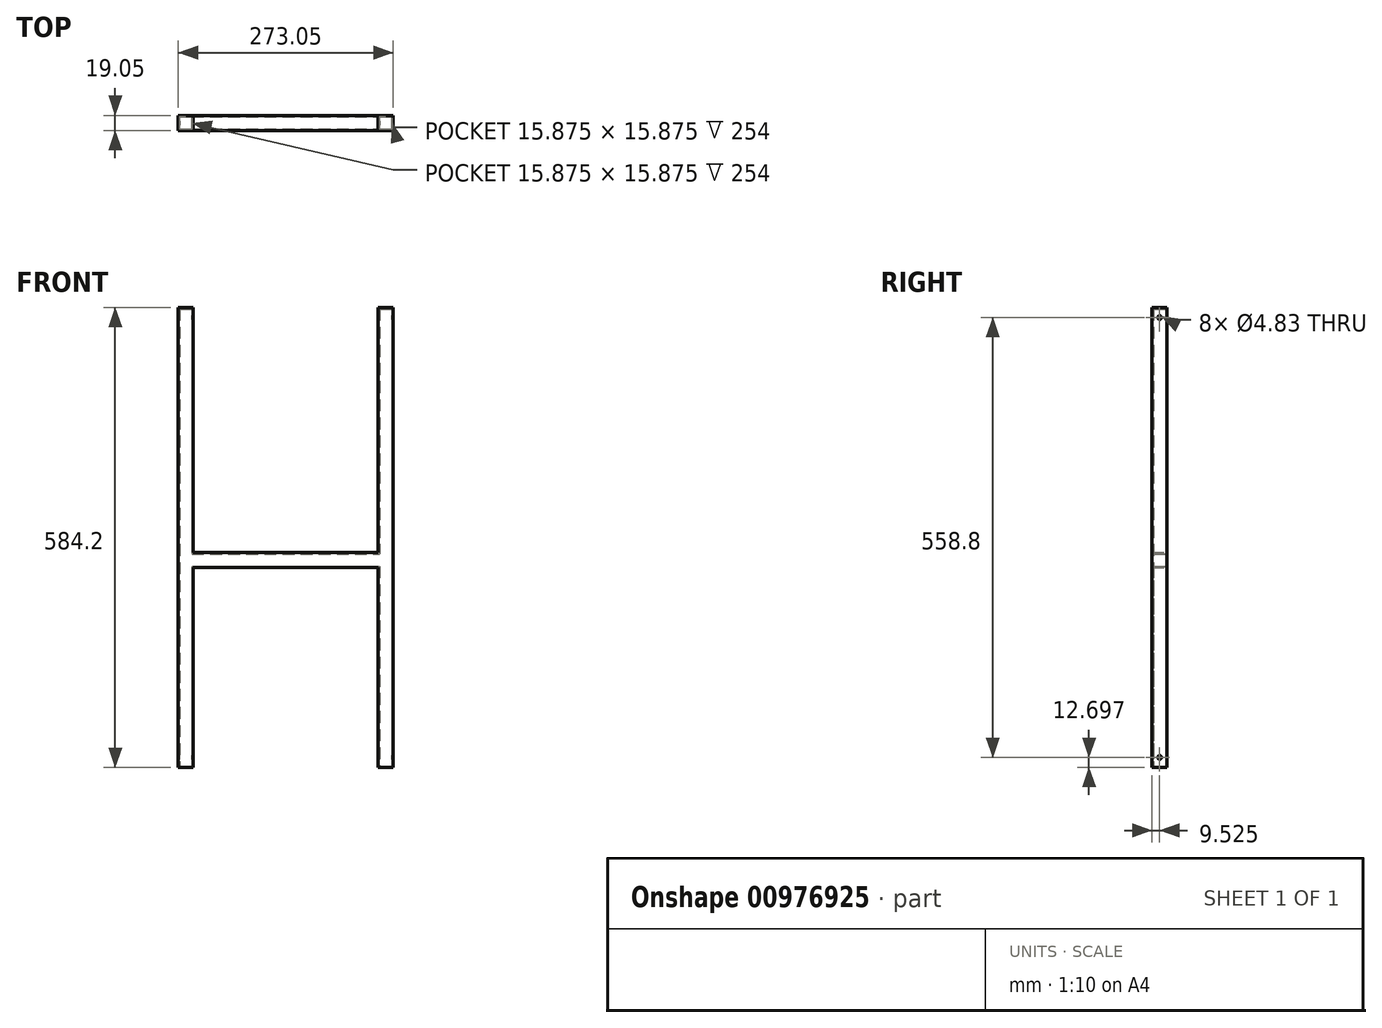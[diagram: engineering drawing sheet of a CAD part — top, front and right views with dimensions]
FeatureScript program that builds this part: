
annotation { "Feature Type Name" : "Feature", "Feature Type Description" : "" }
export const myFeature = defineFeature(function(context is Context, id is Id, definition is map)
    precondition{}
    {
        {
            var Q0;
            Q0=qCreatedBy(makeId("Front.planeOp"),FACE);
            var sketch = newSketch(context, id + "F0", { "sketchPlane" : qUnion([Q0])});
            skLineSegment(sketch, "E0.bottom", {"start": v(-125.54, 190.19) * mm, "end": v(-106.49, 190.19) * mm});
            skLineSegment(sketch, "E0.top", {"start": v(-125.54, -394.01) * mm, "end": v(-106.49, -394.01) * mm});
            skLineSegment(sketch, "E0.left", {"start": v(-125.54, 190.19) * mm, "end": v(-125.54, -394.01) * mm});
            skLineSegment(sketch, "E0.right", {"start": v(-106.49, 190.19) * mm, "end": v(-106.49, -394.01) * mm});
            skLineSegment(sketch, "E1.bottom", {"start": v(128.46, 190.19) * mm, "end": v(147.51, 190.19) * mm});
            skLineSegment(sketch, "E1.top", {"start": v(128.46, -394.01) * mm, "end": v(147.51, -394.01) * mm});
            skLineSegment(sketch, "E1.left", {"start": v(128.46, 190.19) * mm, "end": v(128.46, -394.01) * mm});
            skLineSegment(sketch, "E1.right", {"start": v(147.51, 190.19) * mm, "end": v(147.51, -394.01) * mm});
            skLineSegment(sketch, "E2.bottom", {"start": v(-106.49, -120.96) * mm, "end": v(128.46, -120.96) * mm});
            skLineSegment(sketch, "E2.top", {"start": v(-106.49, -140.01) * mm, "end": v(128.46, -140.01) * mm});
            skLineSegment(sketch, "E2.left", {"start": v(-106.49, -120.96) * mm, "end": v(-106.49, -140.01) * mm});
            skLineSegment(sketch, "E2.right", {"start": v(128.46, -120.96) * mm, "end": v(128.46, -140.01) * mm});
            skSolve(sketch);
        }
        {
            var Q0;
            Q0 = qSketchRegion(id + "F0", true);
            extrude(context, id + "F1", {"entities" : qUnion([Q0]), "depth" : 19.05 * mm, "offsetDistance" : 25.4 * mm});
        }
        {
            var Q0;
            Q0=makeQuery(id+"F1.opExtrude","CAP_FACE",FACE,{"disambiguationData":[OSD([sQuery(id+"F0.wireOp",EDGE,"E0.bottom"),sQuery(id+"F0.wireOp",EDGE,"E0.top"),sQuery(id+"F0.wireOp",EDGE,"E0.left"),sQuery(id+"F0.wireOp",EDGE,"E0.right"),sQuery(id+"F0.wireOp",EDGE,"E1.bottom"),sQuery(id+"F0.wireOp",EDGE,"E1.top"),sQuery(id+"F0.wireOp",EDGE,"E1.left"),sQuery(id+"F0.wireOp",EDGE,"E1.right"),sQuery(id+"F0.wireOp",EDGE,"E2.bottom"),sQuery(id+"F0.wireOp",EDGE,"E2.top")])],"isStart":true});
            var Q1;
            Q1=makeQuery(id+"F1.opExtrude","SWEPT_BODY",BODY,{"disambiguationData":[OSD([sQuery(id+"F0.wireOp",EDGE,"E0.bottom"),sQuery(id+"F0.wireOp",EDGE,"E0.top"),sQuery(id+"F0.wireOp",EDGE,"E0.left"),sQuery(id+"F0.wireOp",EDGE,"E0.right"),sQuery(id+"F0.wireOp",EDGE,"E1.bottom"),sQuery(id+"F0.wireOp",EDGE,"E1.top"),sQuery(id+"F0.wireOp",EDGE,"E1.left"),sQuery(id+"F0.wireOp",EDGE,"E1.right"),sQuery(id+"F0.wireOp",EDGE,"E2.bottom"),sQuery(id+"F0.wireOp",EDGE,"E2.top")])]});
            shell(context, id + "F2", {"isHollow" : true, "entities" : qUnion([Q0]), "parts" : qUnion([Q1]), "thickness" : 1.59 * mm});
        }
        {
            var Q0;
            Q0=makeQuery(id+"F1.opExtrude","SWEPT_FACE",FACE,{"disambiguationData":[OSD([sQuery(id+"F0.wireOp",EDGE,"E1.right")])]});
            var sketch = newSketch(context, id + "F3", { "sketchPlane" : qUnion([Q0])});
            skPoint(sketch, "E3", {"position": v(-9.53, -381.31) * mm});
            skSolve(sketch);
        }
        {
            var Q0;
            Q0=sQuery(id+"F3.wireOp",VERTEX,"E3");
            var Q1;
            Q1=makeQuery(id+"F1.opExtrude","SWEPT_BODY",BODY,{"disambiguationData":[OSD([sQuery(id+"F0.wireOp",EDGE,"E0.bottom"),sQuery(id+"F0.wireOp",EDGE,"E0.top"),sQuery(id+"F0.wireOp",EDGE,"E0.left"),sQuery(id+"F0.wireOp",EDGE,"E0.right"),sQuery(id+"F0.wireOp",EDGE,"E1.bottom"),sQuery(id+"F0.wireOp",EDGE,"E1.top"),sQuery(id+"F0.wireOp",EDGE,"E1.left"),sQuery(id+"F0.wireOp",EDGE,"E1.right"),sQuery(id+"F0.wireOp",EDGE,"E2.bottom"),sQuery(id+"F0.wireOp",EDGE,"E2.top")])]});
            hole(context, id + "F4", {"style" : HoleStyle.SIMPLE, "endStyle" : HoleEndStyle.THROUGH, "holeDiameter" : 4.83 * mm, "majorDiameter" : 6.35 * mm, "isTappedThrough" : true, "tappedDepth" : 12.7 * mm, "tapClearance" : 3, "locations" : qUnion([Q0]), "scope" : qUnion([Q1])});
        }
        {
            var Q0;
            Q0=makeQuery(id+"F1.opExtrude","SWEPT_FACE",FACE,{"disambiguationData":[OSD([sQuery(id+"F0.wireOp",EDGE,"E1.right")])]});
            var sketch = newSketch(context, id + "F5", { "sketchPlane" : qUnion([Q0])});
            skPoint(sketch, "E4", {"position": v(-9.53, 177.49) * mm});
            skSolve(sketch);
        }
        {
            var Q0;
            Q0=sQuery(id+"F5.wireOp",VERTEX,"E4");
            var Q1;
            Q1=makeQuery(id+"F1.opExtrude","SWEPT_BODY",BODY,{"disambiguationData":[OSD([sQuery(id+"F0.wireOp",EDGE,"E0.bottom"),sQuery(id+"F0.wireOp",EDGE,"E0.top"),sQuery(id+"F0.wireOp",EDGE,"E0.left"),sQuery(id+"F0.wireOp",EDGE,"E0.right"),sQuery(id+"F0.wireOp",EDGE,"E1.bottom"),sQuery(id+"F0.wireOp",EDGE,"E1.top"),sQuery(id+"F0.wireOp",EDGE,"E1.left"),sQuery(id+"F0.wireOp",EDGE,"E1.right"),sQuery(id+"F0.wireOp",EDGE,"E2.bottom"),sQuery(id+"F0.wireOp",EDGE,"E2.top")])]});
            hole(context, id + "F6", {"style" : HoleStyle.SIMPLE, "endStyle" : HoleEndStyle.THROUGH, "holeDiameter" : 4.83 * mm, "majorDiameter" : 6.35 * mm, "isTappedThrough" : true, "tappedDepth" : 12.7 * mm, "tapClearance" : 3, "locations" : qUnion([Q0]), "scope" : qUnion([Q1])});
        }
    });
